# Revit family: Б419_RV17_LOD400 (05.11.23)
name_source: partatom
category: Электрооборудование
revit_build: Autodesk Revit 2017 (Build: 20170118_1100(x64)
units: mm (PartAtom-declared; Revit-internal decimal feet)

## family parameters
Всегда вертикально = Нет
Конфигурация панели = Два столбца, слева направо
На основе рабочей плоскости = Да
Общий = Нет
При загрузке вырезать с полостями = Нет
Размер круглого соединителя = Использовать диаметр
Тип детали = Щит
Точка расчета площади = Нет

## types (1)
- Б419
    ADSK_URL страницы изделия = https://stilsoft.ru
    ADSK_Единица измерения = шт.
    ADSK_Завод-изготовитель = ООО «Основа Безопасности»
    ADSK_Количество = 1
    ADSK_Марка = СТВФ.426484.083
    ADSK_Масса = 1
    ADSK_Наименование = Контроллер Б419
    ADSK_Размер_Высота = 32 мм
    ADSK_Размер_Глубина = 100 мм
    ADSK_Размер_Длина = 181 мм
    d_короба = 20 мм
    Интерфейс для подключения внешних устройств = RS-485
    Информационная ёмкость (количество подключаемых шлейфов сигнализации), не более, шт. = 8
    Количество выходов типа «открытый коллектор», не более, шт. = 4
    Количество выходов типа «сухой контакт», не более, шт. = 2
    Количество подключаемых исполнительных устройств, не более, шт. = 6
    Количество подключаемых считывателей STS-705P по интерфейсу RS-485, не более, шт. = 2
    Максимальное количество извещателей охранной сигнализации на 1 шлейф сигнализации, питающихся от шлейфа, не более, шт = 20
    Максимальный ток коммутации выходов типа «открытый коллектор» напряжением до 50В постоянного тока, не более, А = 1 А
    Максимальный ток коммутации выходов типа «сухой контакт» напряжением 250В (переменного тока) , не более, А = 10 А
    Максимальный ток коммутации выходов типа «сухой контакт» напряжением 28В (постоянного тока), не более, А = 12 А
    Напряжение = 12
    Отметка по умолчанию = 1219 мм
    Потребляемый ток, не более, А = 0 А
    Предельное значение сопротивления проводов ШС, кОм = 0.1
    Стандарт интерфейса связи = 10 Base-T Ethernet (гнездо RJ-45)
